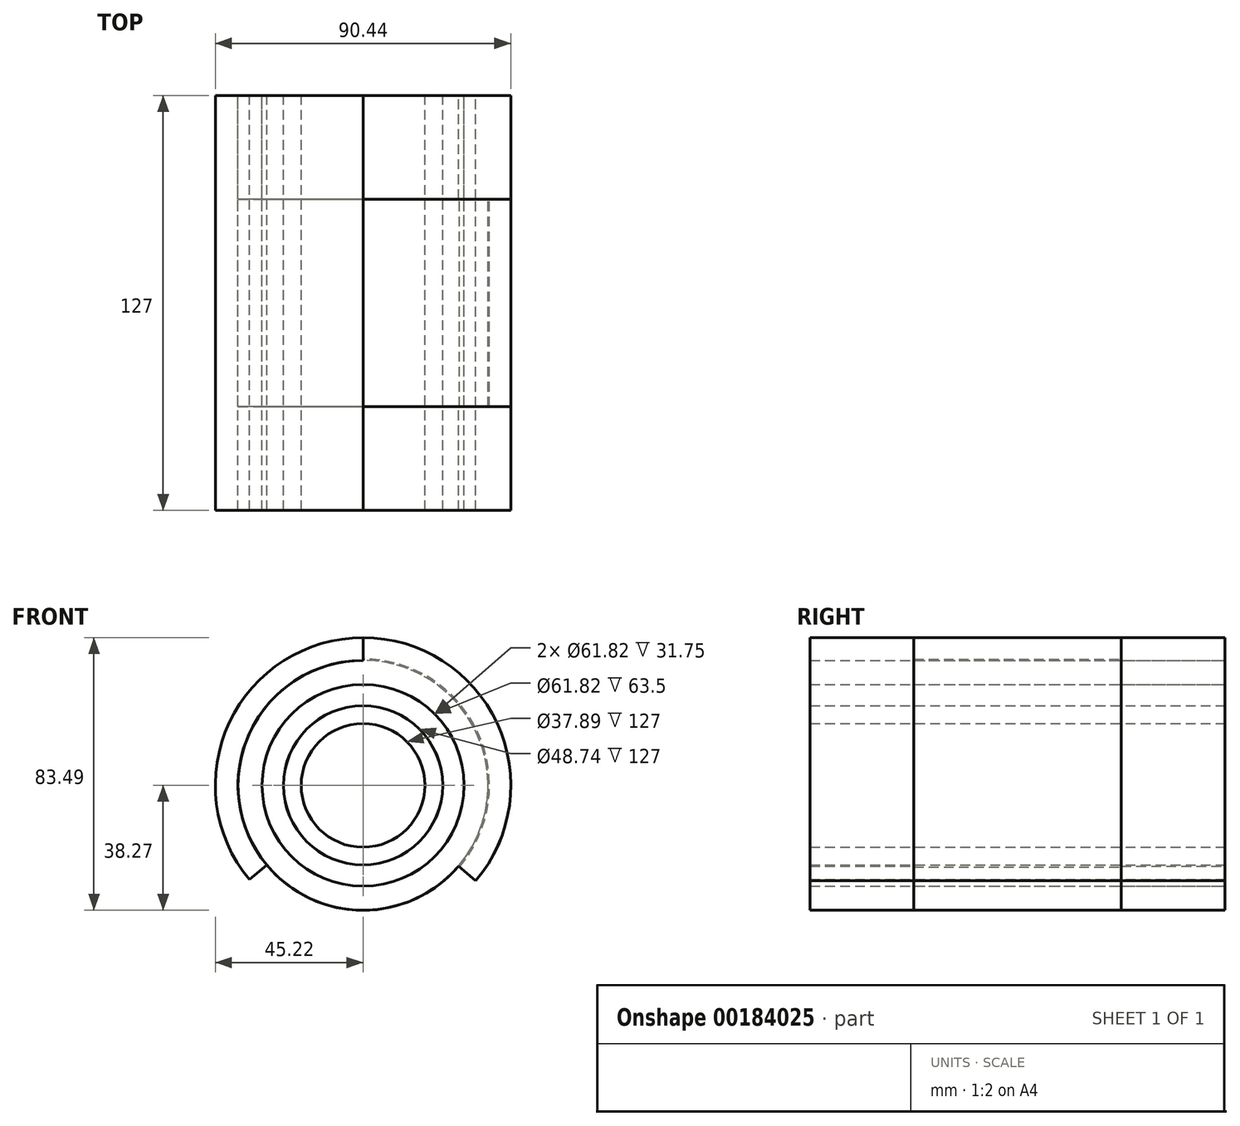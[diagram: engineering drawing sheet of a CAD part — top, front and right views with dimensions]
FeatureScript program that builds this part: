
annotation { "Feature Type Name" : "Feature", "Feature Type Description" : "" }
export const myFeature = defineFeature(function(context is Context, id is Id, definition is map)
    precondition{}
    {
        {
            var Q0;
            Q0=qCreatedBy(makeId("Front.planeOp"),FACE);
            var sketch = newSketch(context, id + "F0", { "sketchPlane" : qUnion([Q0])});
            skArc(sketch, "E0", {"start": v(0, 45.22) * mm, "mid": v(-40.93, 19.24) * mm, "end": v(-34.82, -28.86) * mm});
            skArc(sketch, "E1", {"start": v(0, 38.27) * mm, "mid": v(-34.63, 16.28) * mm, "end": v(-29.46, -24.42) * mm});
            skCircle(sketch, "E2", {"center": v(0, 0) * mm, "radius": 30.91 * mm});
            skCircle(sketch, "E3", {"center": v(0, 0) * mm, "radius": 24.37 * mm});
            skLineSegment(sketch, "E4.trimOffspring", {"start": v(0, 38.27) * mm, "end": v(0, 54.76) * mm});
            skLineSegment(sketch, "E5.trimOffspring", {"start": v(-29.46, -24.42) * mm, "end": v(-34.82, -28.86) * mm});
            skCircle(sketch, "E6", {"center": v(0, 0) * mm, "radius": 38.27 * mm});
            skSolve(sketch);
        }
        {
            var Q0;
            {var subQ0=sQuery(id+"F0.wireOp",EDGE,"E0");Q0=makeQuery(id+"F0.imprint","IMPRINT",FACE,{"disambiguationData":[TD([[makeQuery(id+"F0.imprint","IMPRINT",EDGE,{"derivedFrom":subQ0}),1.0]])]});}
            var Q1;
            Q1=makeQuery(id+"F0.imprint","IMPRINT",FACE,{"disambiguationData":[TD([[makeQuery(id+"F0.imprint","IMPRINT",EDGE,{"derivedFrom":sQuery(id+"F0.wireOp",EDGE,"E2")}),1.0]])]});
            extrude(context, id + "F1", {"entities" : qUnion([Q0, Q1]), "depth" : 63.5 * mm, "hasSecondDirection" : true, "secondDirectionOppositeDirection" : true, "secondDirectionDepth" : 63.5 * mm});
        }
        {
            var Q0;
            Q0=makeQuery(id+"F0.imprint","IMPRINT",FACE,{"disambiguationData":[TD([[makeQuery(id+"F0.imprint","IMPRINT",EDGE,{"derivedFrom":sQuery(id+"F0.wireOp",EDGE,"E2")}),-1.0]])]});
            extrude(context, id + "F2", {"entities" : qUnion([Q0]), "depth" : 31.75 * mm, "hasSecondDirection" : true, "secondDirectionOppositeDirection" : true, "secondDirectionDepth" : 31.75 * mm});
        }
        {
            var Q0;
            Q0=qCreatedBy(makeId("Front.planeOp"),FACE);
            var sketch = newSketch(context, id + "F3", { "sketchPlane" : qUnion([Q0])});
            skArc(sketch, "E7", {"start": v(34.5, -29.24) * mm, "mid": v(41.03, 19.01) * mm, "end": v(0, 45.22) * mm});
            skLineSegment(sketch, "E8", {"start": v(29.2, -24.74) * mm, "end": v(34.5, -29.24) * mm});
            skArc(sketch, "E9", {"start": v(0, 38.27) * mm, "mid": v(-34.72, -16.09) * mm, "end": v(29.2, -24.74) * mm});
            skCircle(sketch, "E10", {"center": v(0, 0) * mm, "radius": 30.91 * mm});
            skLineSegment(sketch, "E11.trimOffspring", {"start": v(0, 38.27) * mm, "end": v(0, 45.22) * mm});
            skSolve(sketch);
        }
        {
            var Q0;
            Q0=makeQuery(id+"F3.imprint","IMPRINT",FACE,{"disambiguationData":[TD([[makeQuery(id+"F3.imprint","IMPRINT",EDGE,{"derivedFrom":sQuery(id+"F3.wireOp",EDGE,"E7")}),1.0]])]});
            extrude(context, id + "F4", {"entities" : qUnion([Q0]), "depth" : 31.75 * mm});
        }
        {
            var Q0;
            Q0=makeQuery(id+"F4.opExtrude","SWEPT_BODY",BODY,{"disambiguationData":[OSD([sQuery(id+"F3.wireOp",EDGE,"E7"),sQuery(id+"F3.wireOp",EDGE,"E8"),sQuery(id+"F3.wireOp",EDGE,"E9"),sQuery(id+"F3.wireOp",EDGE,"E10"),sQuery(id+"F3.wireOp",EDGE,"E11.trimOffspring")])]});
            transform(context, id + "F5", {"entities" : qUnion([Q0]), "transformType" : TransformType.TRANSLATION_3D, "dx" : 0 * mm, "dy" : -31.75 * mm, "dz" : 0 * mm, "makeCopy" : false});
        }
        {
            var Q0;
            Q0=makeQuery(id+"F4.opExtrude","SWEPT_BODY",BODY,{"disambiguationData":[OSD([sQuery(id+"F3.wireOp",EDGE,"E7"),sQuery(id+"F3.wireOp",EDGE,"E8"),sQuery(id+"F3.wireOp",EDGE,"E9"),sQuery(id+"F3.wireOp",EDGE,"E10"),sQuery(id+"F3.wireOp",EDGE,"E11.trimOffspring")])]});
            transform(context, id + "F6", {"entities" : qUnion([Q0]), "transformType" : TransformType.COPY});
        }
        {
            var Q0;
            Q0=makeQuery(id+"F4.opExtrude","SWEPT_BODY",BODY,{"disambiguationData":[OSD([sQuery(id+"F3.wireOp",EDGE,"E7"),sQuery(id+"F3.wireOp",EDGE,"E8"),sQuery(id+"F3.wireOp",EDGE,"E9"),sQuery(id+"F3.wireOp",EDGE,"E10"),sQuery(id+"F3.wireOp",EDGE,"E11.trimOffspring")])]});
            transform(context, id + "F7", {"entities" : qUnion([Q0]), "transformType" : TransformType.TRANSLATION_3D, "dx" : 0 * mm, "dy" : 95.25 * mm, "dz" : 0 * mm, "makeCopy" : false});
        }
        {
            var Q0;
            Q0=qCreatedBy(makeId("Front.planeOp"),FACE);
            var sketch = newSketch(context, id + "F8", { "sketchPlane" : qUnion([Q0])});
            skArc(sketch, "E12", {"start": v(29.5, -24.99) * mm, "mid": v(35.08, 16.26) * mm, "end": v(0, 38.66) * mm});
            skArc(sketch, "E13", {"start": v(34.5, -29.23) * mm, "mid": v(41.03, 19.02) * mm, "end": v(0, 45.22) * mm});
            skLineSegment(sketch, "E14", {"start": v(0, 38.66) * mm, "end": v(0, 45.22) * mm});
            skLineSegment(sketch, "E15", {"start": v(29.5, -24.99) * mm, "end": v(34.5, -29.23) * mm});
            skSolve(sketch);
        }
        {
            var Q0;
            Q0=makeQuery(id+"F8.imprint","IMPRINT",FACE,{"disambiguationData":[TD([[makeQuery(id+"F8.imprint","IMPRINT",EDGE,{"derivedFrom":sQuery(id+"F8.wireOp",EDGE,"E12")}),-1.0]])]});
            extrude(context, id + "F9", {"entities" : qUnion([Q0]), "depth" : 31.75 * mm, "hasSecondDirection" : true, "secondDirectionOppositeDirection" : true, "secondDirectionDepth" : 31.75 * mm});
        }
        {
            var Q0;
            Q0=qCreatedBy(makeId("Front.planeOp"),FACE);
            var sketch = newSketch(context, id + "F10", { "sketchPlane" : qUnion([Q0])});
            skCircle(sketch, "E16", {"center": v(0, 0) * mm, "radius": 24.35 * mm});
            skCircle(sketch, "E17", {"center": v(0, 0) * mm, "radius": 18.95 * mm});
            skSolve(sketch);
        }
        {
            var Q0;
            Q0=makeQuery(id+"F10.imprint","IMPRINT",FACE,{"disambiguationData":[TD([[makeQuery(id+"F10.imprint","IMPRINT",EDGE,{"derivedFrom":sQuery(id+"F10.wireOp",EDGE,"E16")}),1.0]])]});
            extrude(context, id + "F11", {"entities" : qUnion([Q0]), "depth" : 63.5 * mm, "hasSecondDirection" : true, "secondDirectionOppositeDirection" : true, "secondDirectionDepth" : 63.5 * mm});
        }
    });
